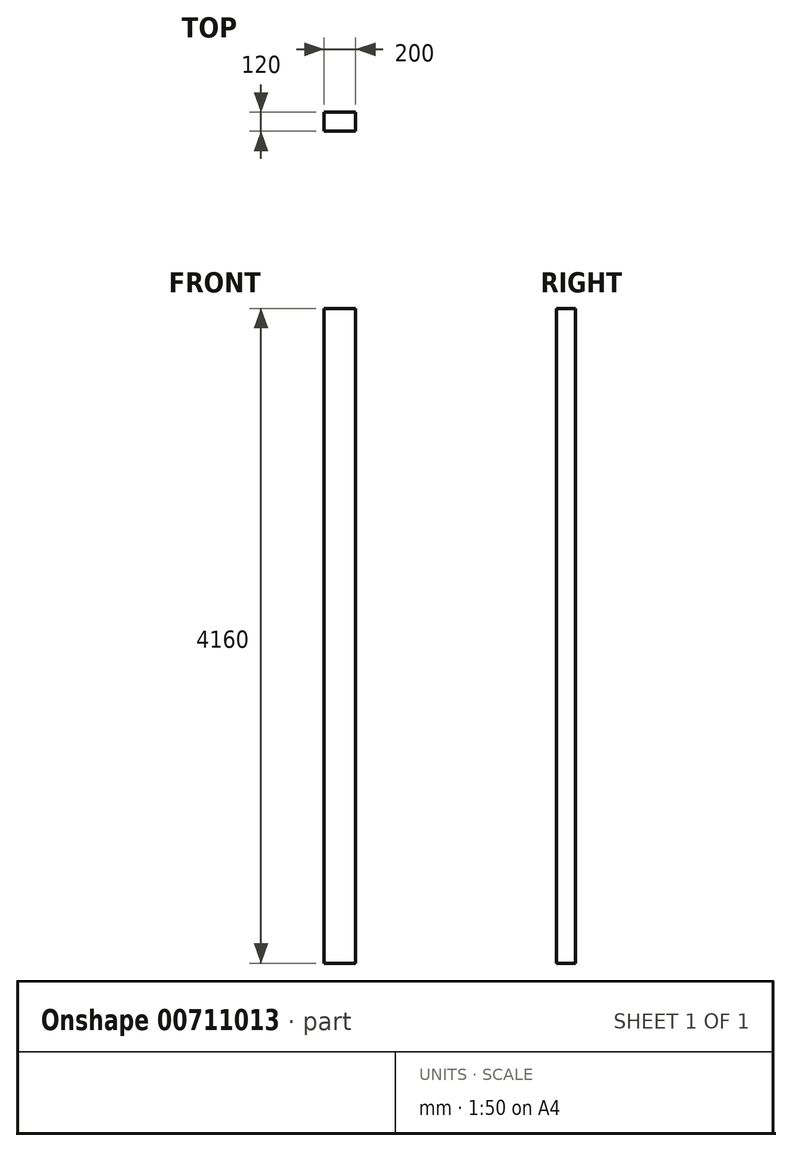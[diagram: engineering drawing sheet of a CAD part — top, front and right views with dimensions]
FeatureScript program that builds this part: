
annotation { "Feature Type Name" : "Feature", "Feature Type Description" : "" }
export const myFeature = defineFeature(function(context is Context, id is Id, definition is map)
    precondition{}
    {
        {
            var Q0;
            Q0=qCreatedBy(makeId("Top.planeOp"),FACE);
            var sketch = newSketch(context, id + "F0", { "sketchPlane" : qUnion([Q0])});
            skLineSegment(sketch, "E0.bottom", {"start": v(-94.09, 36.7) * mm, "end": v(105.91, 36.7) * mm});
            skLineSegment(sketch, "E0.top", {"start": v(-94.09, -83.3) * mm, "end": v(105.91, -83.3) * mm});
            skLineSegment(sketch, "E0.left", {"start": v(-94.09, 36.7) * mm, "end": v(-94.09, -83.3) * mm});
            skLineSegment(sketch, "E0.right", {"start": v(105.91, 36.7) * mm, "end": v(105.91, -83.3) * mm});
            skSolve(sketch);
        }
        {
            var Q0;
            Q0=makeQuery(id+"F0.imprint","IMPRINT",FACE,{"disambiguationData":[TD([[makeQuery(id+"F0.imprint","IMPRINT",EDGE,{"derivedFrom":sQuery(id+"F0.wireOp",EDGE,"E0.bottom")}),-1.0]])]});
            extrude(context, id + "F1", {"entities" : qUnion([Q0]), "depth" : 4160 * mm, "offsetDistance" : 25 * mm});
        }
    });
